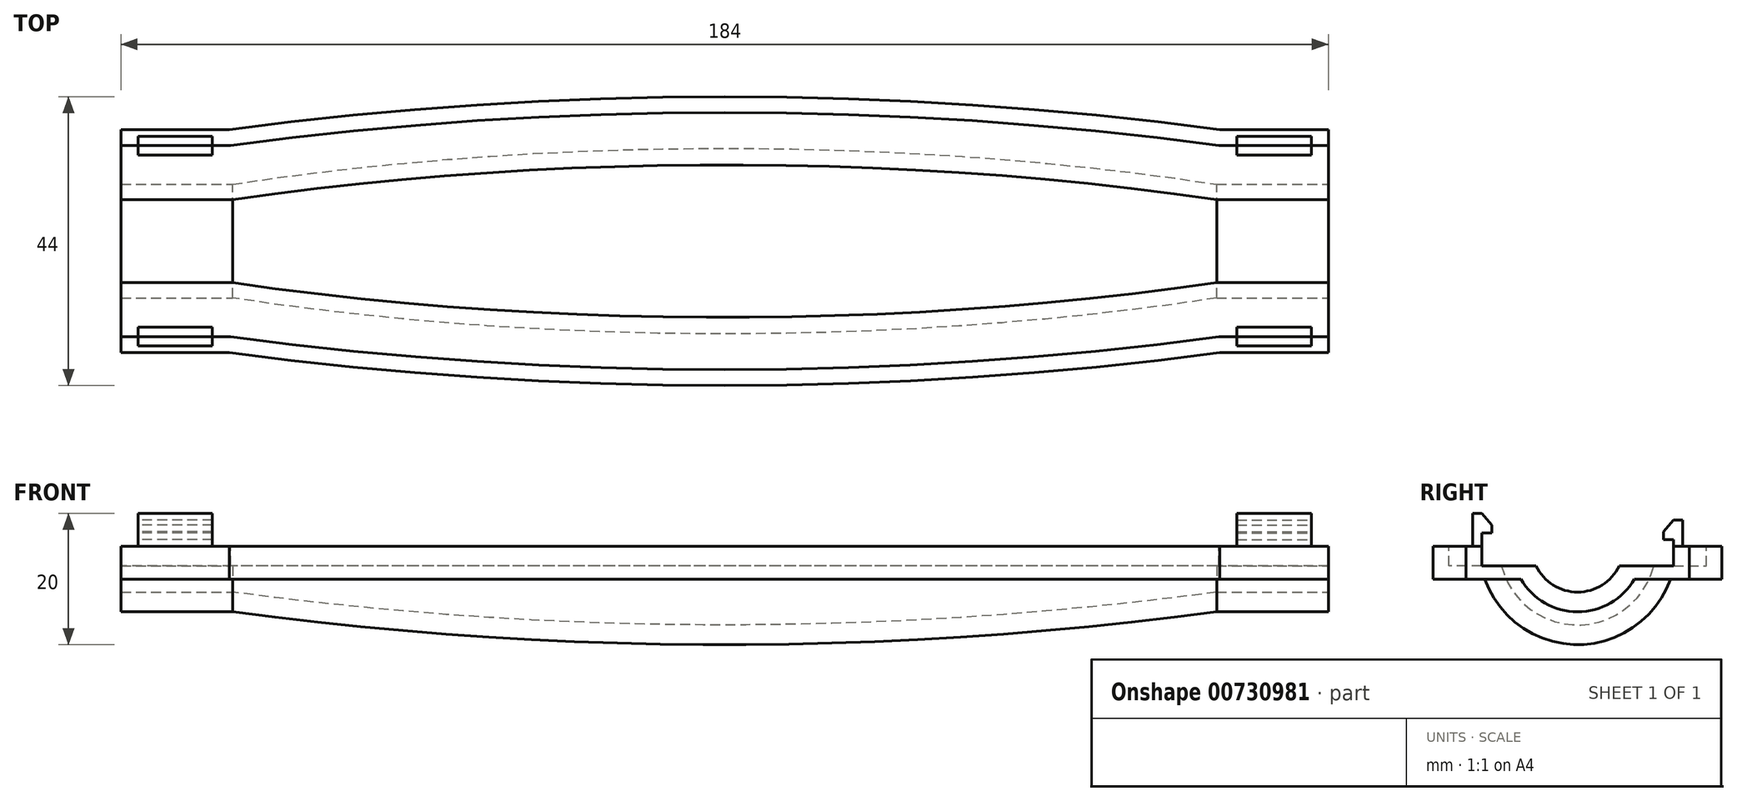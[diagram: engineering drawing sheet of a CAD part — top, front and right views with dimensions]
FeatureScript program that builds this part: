
annotation { "Feature Type Name" : "Feature", "Feature Type Description" : "" }
export const myFeature = defineFeature(function(context is Context, id is Id, definition is map)
    precondition{}
    {
        {
            var Q0;
            Q0=qCreatedBy(makeId("Top.planeOp"),FACE);
            var sketch = newSketch(context, id + "F0", { "sketchPlane" : qUnion([Q0])});
            skLineSegment(sketch, "E0", {"start": v(0, 0) * mm, "end": v(0, 12) * mm, "construction": true});
            skLineSegment(sketch, "E1", {"start": v(0, 0) * mm, "end": v(0, -12) * mm, "construction": true});
            skLineSegment(sketch, "E2", {"start": v(0, 0) * mm, "end": v(-75, 0) * mm, "construction": true});
            skLineSegment(sketch, "E3", {"start": v(0, 0) * mm, "end": v(75, 0) * mm, "construction": true});
            skLineSegment(sketch, "E4", {"start": v(-75, 0) * mm, "end": v(-75, 7) * mm, "construction": true});
            skLineSegment(sketch, "E5", {"start": v(75, 0) * mm, "end": v(75, 7) * mm, "construction": true});
            skArc(sketch, "E6", {"start": v(75, 7) * mm, "mid": v(0, 12) * mm, "end": v(-75, 7) * mm});
            skLineSegment(sketch, "E7", {"start": v(75, 7) * mm, "end": v(92, 7) * mm});
            skLineSegment(sketch, "E8", {"start": v(-75, 7) * mm, "end": v(-92, 7) * mm});
            skLineSegment(sketch, "E9", {"start": v(-92, 7) * mm, "end": v(-92, 10) * mm});
            skLineSegment(sketch, "E10", {"start": v(-92, 10) * mm, "end": v(-75, 10) * mm});
            skLineSegment(sketch, "E11", {"start": v(92, 7) * mm, "end": v(92, 10) * mm});
            skLineSegment(sketch, "E12", {"start": v(92, 10) * mm, "end": v(75, 10) * mm});
            skLineSegment(sketch, "E13", {"start": v(0, 12) * mm, "end": v(0, 15) * mm, "construction": true});
            skArc(sketch, "E14", {"start": v(75, 10) * mm, "mid": v(0, 15) * mm, "end": v(-75, 10) * mm});
            skSolve(sketch);
        }
        {
            var Q0;
            Q0=makeQuery(id+"F0.imprint","IMPRINT",FACE,{"disambiguationData":[TD([[makeQuery(id+"F0.imprint","IMPRINT",EDGE,{"derivedFrom":sQuery(id+"F0.wireOp",EDGE,"E6")}),-1.0]])]});
            var Q1;
            Q1=sQuery(id+"F0.wireOp",EDGE,"E2");
            revolve(context, id + "F1", {"surfaceOperationType" : NewSurfaceOperationType.NEW, "entities" : qUnion([Q0]), "axis" : qUnion([Q1]), "revolveType" : RevolveType.ONE_DIRECTION, "angle" : 180 * degree});
        }
        {
            var Q0;
            Q0=makeQuery(id+"F1.opRevolve","CAP_FACE",FACE,{"disambiguationData":[OSD([sQuery(id+"F0.wireOp",EDGE,"E6"),sQuery(id+"F0.wireOp",EDGE,"E7"),sQuery(id+"F0.wireOp",EDGE,"E8"),sQuery(id+"F0.wireOp",EDGE,"E9"),sQuery(id+"F0.wireOp",EDGE,"E10"),sQuery(id+"F0.wireOp",EDGE,"E11"),sQuery(id+"F0.wireOp",EDGE,"E12"),sQuery(id+"F0.wireOp",EDGE,"E14")])],"isStart":true});
            var sketch = newSketch(context, id + "F2", { "sketchPlane" : qUnion([Q0])});
            skLineSegment(sketch, "E15.0", {"start": v(-92, 17) * mm, "end": v(-75.47, 17) * mm});
            skArc(sketch, "E15.1", {"start": v(75.47, 17) * mm, "mid": v(0, 22) * mm, "end": v(-75.47, 17) * mm});
            skLineSegment(sketch, "E15.2", {"start": v(92, 17) * mm, "end": v(75.47, 17) * mm});
            skLineSegment(sketch, "E16", {"start": v(-92, 17) * mm, "end": v(-92, 10) * mm});
            skLineSegment(sketch, "E17", {"start": v(92, 17) * mm, "end": v(92, 10) * mm});
            skSolve(sketch);
        }
        {
            var Q0;
            Q0=makeQuery(id+"F2.imprint","IMPRINT",FACE,{"disambiguationData":[TD([[makeQuery(id+"F2.imprint","IMPRINT",EDGE,{"derivedFrom":makeQuery(id+"F1.opRevolve","CAP_EDGE",EDGE,{"disambiguationData":[OSD([sQuery(id+"F0.wireOp",EDGE,"E6")])],"isStart":true})}),-1.0]])]});
            var Q1;
            Q1=makeQuery(id+"F2.imprint","IMPRINT",FACE,{"disambiguationData":[TD([[makeQuery(id+"F2.imprint","IMPRINT",EDGE,{"derivedFrom":sQuery(id+"F2.wireOp",EDGE,"E15.0")}),-1.0]])]});
            extrude(context, id + "F3", {"entities" : qUnion([Q0, Q1]), "operationType" : NewBodyOperationType.ADD, "oppositeDirection" : true, "depth" : 5 * mm, "offsetDistance" : 25 * mm});
        }
        {
            var Q0;
            Q0=makeQuery(id+"F1.opRevolve","CAP_FACE",FACE,{"disambiguationData":[OSD([sQuery(id+"F0.wireOp",EDGE,"E6"),sQuery(id+"F0.wireOp",EDGE,"E7"),sQuery(id+"F0.wireOp",EDGE,"E8"),sQuery(id+"F0.wireOp",EDGE,"E9"),sQuery(id+"F0.wireOp",EDGE,"E10"),sQuery(id+"F0.wireOp",EDGE,"E11"),sQuery(id+"F0.wireOp",EDGE,"E12"),sQuery(id+"F0.wireOp",EDGE,"E14")])],"isStart":false});
            var sketch = newSketch(context, id + "F4", { "sketchPlane" : qUnion([Q0])});
            skLineSegment(sketch, "E18.0", {"start": v(-92, -17) * mm, "end": v(-75.47, -17) * mm});
            skArc(sketch, "E18.1", {"start": v(75.47, -17) * mm, "mid": v(0, -22) * mm, "end": v(-75.47, -17) * mm});
            skLineSegment(sketch, "E18.2", {"start": v(92, -17) * mm, "end": v(75.47, -17) * mm});
            skLineSegment(sketch, "E19", {"start": v(-92, -17) * mm, "end": v(-92, -10) * mm});
            skLineSegment(sketch, "E20", {"start": v(92, -17) * mm, "end": v(92, -10) * mm});
            skSolve(sketch);
        }
        {
            var Q0;
            Q0=makeQuery(id+"F4.imprint","IMPRINT",FACE,{"disambiguationData":[TD([[makeQuery(id+"F4.imprint","IMPRINT",EDGE,{"derivedFrom":makeQuery(id+"F1.opRevolve","CAP_EDGE",EDGE,{"disambiguationData":[OSD([sQuery(id+"F0.wireOp",EDGE,"E6")])],"isStart":false})}),1.0]])]});
            var Q1;
            Q1=makeQuery(id+"F4.imprint","IMPRINT",FACE,{"disambiguationData":[TD([[makeQuery(id+"F4.imprint","IMPRINT",EDGE,{"derivedFrom":sQuery(id+"F4.wireOp",EDGE,"E18.0")}),1.0]])]});
            extrude(context, id + "F5", {"entities" : qUnion([Q0, Q1]), "operationType" : NewBodyOperationType.ADD, "oppositeDirection" : true, "depth" : 5 * mm, "offsetDistance" : 25 * mm});
        }
        {
            var Q0;
            {var subQ0=sQuery(id+"F0.wireOp",EDGE,"E11");var subQ1=sQuery(id+"F0.wireOp",EDGE,"E9");var subQ2=sQuery(id+"F0.wireOp",EDGE,"E8");var subQ3=sQuery(id+"F0.wireOp",EDGE,"E7");var subQ4=sQuery(id+"F0.wireOp",EDGE,"E6");Q0=makeQuery(id+"F3.boolean.opBoolean","MERGE",FACE,{"derivedFrom":[makeQuery(id+"F1.opRevolve","CAP_FACE",FACE,{"disambiguationData":[OSD([subQ4,subQ3,subQ2,subQ1,sQuery(id+"F0.wireOp",EDGE,"E10"),subQ0,sQuery(id+"F0.wireOp",EDGE,"E12"),sQuery(id+"F0.wireOp",EDGE,"E14")])],"isStart":true}),makeQuery(id+"F3.opExtrude","CAP_FACE",FACE,{"disambiguationData":[OSD([subQ4,subQ3,subQ2,subQ1,subQ0,sQuery(id+"F2.wireOp",EDGE,"E15.0"),sQuery(id+"F2.wireOp",EDGE,"E15.1"),sQuery(id+"F2.wireOp",EDGE,"E15.2"),sQuery(id+"F2.wireOp",EDGE,"E16"),sQuery(id+"F2.wireOp",EDGE,"E17")])],"isStart":true})]});}
            var sketch = newSketch(context, id + "F6", { "sketchPlane" : qUnion([Q0])});
            skLineSegment(sketch, "E21.0", {"start": v(-92, 14.6) * mm, "end": v(-75.3, 14.6) * mm});
            skArc(sketch, "E21.1", {"start": v(75.3, 14.6) * mm, "mid": v(0, 19.6) * mm, "end": v(-75.3, 14.6) * mm});
            skLineSegment(sketch, "E21.2", {"start": v(92, 14.6) * mm, "end": v(75.3, 14.6) * mm});
            skArc(sketch, "E22.0", {"start": v(75, 8.82) * mm, "mid": v(0, 13.8) * mm, "end": v(-75, 8.82) * mm});
            skLineSegment(sketch, "E23", {"start": v(-75, 7) * mm, "end": v(-75, 8.82) * mm});
            skLineSegment(sketch, "E24", {"start": v(75, 7) * mm, "end": v(75, 8.82) * mm});
            skSolve(sketch);
        }
        {
            var Q0;
            {var subQ7=sQuery(id+"F6.wireOp",EDGE,"E21.0");Q0=makeQuery(id+"F6.imprint","IMPRINT",FACE,{"disambiguationData":[TD([[makeQuery(id+"F6.imprint","IMPRINT",EDGE,{"derivedFrom":subQ7}),-1.0]])]});}
            extrude(context, id + "F7", {"entities" : qUnion([Q0]), "operationType" : NewBodyOperationType.REMOVE, "oppositeDirection" : true, "depth" : 3 * mm, "offsetDistance" : 25 * mm});
        }
        {
            var Q0;
            {var subQ0=sQuery(id+"F0.wireOp",EDGE,"E9");Q0=makeQuery(id+"F5.boolean.opBoolean","MERGE",FACE,{"derivedFrom":[makeQuery(id+"F3.boolean.opBoolean","MERGE",FACE,{"derivedFrom":[makeQuery(id+"F1.opRevolve","SWEPT_FACE",FACE,{"disambiguationData":[OSD([subQ0])]}),makeQuery(id+"F3.opExtrude","SWEPT_FACE",FACE,{"disambiguationData":[OSD([subQ0,sQuery(id+"F2.wireOp",EDGE,"E16")])]})]}),makeQuery(id+"F5.opExtrude","SWEPT_FACE",FACE,{"disambiguationData":[OSD([subQ0,sQuery(id+"F4.wireOp",EDGE,"E19")])]})]});}
            var sketch = newSketch(context, id + "F8", { "sketchPlane" : qUnion([Q0])});
            skLineSegment(sketch, "E25", {"start": v(-7, -3) * mm, "end": v(-6.32, -3) * mm});
            skSolve(sketch);
        }
        {
            var Q0;
            {var subQ0=sQuery(id+"F8.wireOp",EDGE,"E25");Q0=makeQuery(id+"F8.imprint","IMPRINT",FACE,{"disambiguationData":[TD([[makeQuery(id+"F8.imprint","IMPRINT",EDGE,{"derivedFrom":subQ0}),1.0]])]});}
            extrude(context, id + "F9", {"entities" : qUnion([Q0]), "operationType" : NewBodyOperationType.REMOVE, "oppositeDirection" : true, "depth" : 17 * mm, "offsetDistance" : 25 * mm});
        }
        {
            var Q0;
            {var subQ0=sQuery(id+"F0.wireOp",EDGE,"E11");Q0=makeQuery(id+"F5.boolean.opBoolean","MERGE",FACE,{"derivedFrom":[makeQuery(id+"F3.boolean.opBoolean","MERGE",FACE,{"derivedFrom":[makeQuery(id+"F1.opRevolve","SWEPT_FACE",FACE,{"disambiguationData":[OSD([subQ0])]}),makeQuery(id+"F3.opExtrude","SWEPT_FACE",FACE,{"disambiguationData":[OSD([subQ0,sQuery(id+"F2.wireOp",EDGE,"E17")])]})]}),makeQuery(id+"F5.opExtrude","SWEPT_FACE",FACE,{"disambiguationData":[OSD([subQ0,sQuery(id+"F4.wireOp",EDGE,"E20")])]})]});}
            var sketch = newSketch(context, id + "F10", { "sketchPlane" : qUnion([Q0])});
            skLineSegment(sketch, "E26", {"start": v(7, -3) * mm, "end": v(6.32, -3) * mm});
            skSolve(sketch);
        }
        {
            var Q0;
            {var subQ0=sQuery(id+"F10.wireOp",EDGE,"E26");Q0=makeQuery(id+"F10.imprint","IMPRINT",FACE,{"disambiguationData":[TD([[makeQuery(id+"F10.imprint","IMPRINT",EDGE,{"derivedFrom":subQ0}),-1.0]])]});}
            extrude(context, id + "F11", {"entities" : qUnion([Q0]), "operationType" : NewBodyOperationType.REMOVE, "oppositeDirection" : true, "depth" : 17 * mm, "offsetDistance" : 25 * mm});
        }
        {
            var Q0;
            {var subQ0=sQuery(id+"F0.wireOp",EDGE,"E11");var subQ1=sQuery(id+"F0.wireOp",EDGE,"E9");var subQ2=sQuery(id+"F0.wireOp",EDGE,"E8");var subQ3=sQuery(id+"F0.wireOp",EDGE,"E7");var subQ4=sQuery(id+"F0.wireOp",EDGE,"E6");Q0=makeQuery(id+"F5.boolean.opBoolean","MERGE",FACE,{"derivedFrom":[makeQuery(id+"F1.opRevolve","CAP_FACE",FACE,{"disambiguationData":[OSD([subQ4,subQ3,subQ2,subQ1,sQuery(id+"F0.wireOp",EDGE,"E10"),subQ0,sQuery(id+"F0.wireOp",EDGE,"E12"),sQuery(id+"F0.wireOp",EDGE,"E14")])],"isStart":false}),makeQuery(id+"F5.opExtrude","CAP_FACE",FACE,{"disambiguationData":[OSD([subQ4,subQ3,subQ2,subQ1,subQ0,sQuery(id+"F4.wireOp",EDGE,"E18.0"),sQuery(id+"F4.wireOp",EDGE,"E18.1"),sQuery(id+"F4.wireOp",EDGE,"E18.2"),sQuery(id+"F4.wireOp",EDGE,"E19"),sQuery(id+"F4.wireOp",EDGE,"E20")])],"isStart":true})]});}
            var sketch = newSketch(context, id + "F12", { "sketchPlane" : qUnion([Q0])});
            skLineSegment(sketch, "E27.0", {"start": v(-92, -14.6) * mm, "end": v(-75.3, -14.6) * mm});
            skArc(sketch, "E27.1", {"start": v(75.3, -14.6) * mm, "mid": v(0, -19.6) * mm, "end": v(-75.3, -14.6) * mm});
            skLineSegment(sketch, "E27.2", {"start": v(92, -14.6) * mm, "end": v(75.3, -14.6) * mm});
            skLineSegment(sketch, "E28.0", {"start": v(-75.12, -8.8) * mm, "end": v(-92, -8.8) * mm});
            skArc(sketch, "E28.1", {"start": v(75.12, -8.8) * mm, "mid": v(0, -13.8) * mm, "end": v(-75.12, -8.8) * mm});
            skLineSegment(sketch, "E28.2", {"start": v(75.12, -8.8) * mm, "end": v(92, -8.8) * mm});
            skLineSegment(sketch, "E29", {"start": v(75, -7) * mm, "end": v(75, -8.82) * mm});
            skLineSegment(sketch, "E30", {"start": v(-75, -7) * mm, "end": v(-75, -8.82) * mm});
            skSolve(sketch);
        }
        {
            var Q0;
            {var subQ3=sQuery(id+"F12.wireOp",EDGE,"E28.0");Q0=makeQuery(id+"F12.imprint","IMPRINT",FACE,{"disambiguationData":[TD([[makeQuery(id+"F12.imprint","IMPRINT",EDGE,{"derivedFrom":subQ3}),-1.0]])]});}
            var Q1;
            {var subQ2=sQuery(id+"F12.wireOp",EDGE,"E27.0");Q1=makeQuery(id+"F12.imprint","IMPRINT",FACE,{"disambiguationData":[TD([[makeQuery(id+"F12.imprint","IMPRINT",EDGE,{"derivedFrom":subQ2}),1.0]])]});}
            var Q2;
            {var subQ4=sQuery(id+"F12.wireOp",EDGE,"E28.2");Q2=makeQuery(id+"F12.imprint","IMPRINT",FACE,{"disambiguationData":[TD([[makeQuery(id+"F12.imprint","IMPRINT",EDGE,{"derivedFrom":subQ4}),1.0]])]});}
            extrude(context, id + "F13", {"entities" : qUnion([Q0, Q1, Q2]), "operationType" : NewBodyOperationType.REMOVE, "oppositeDirection" : true, "depth" : 3 * mm, "offsetDistance" : 25 * mm});
        }
        {
            var Q0;
            {var subQ0=sQuery(id+"F0.wireOp",EDGE,"E9");Q0=makeQuery(id+"F5.boolean.opBoolean","MERGE",FACE,{"derivedFrom":[makeQuery(id+"F3.boolean.opBoolean","MERGE",FACE,{"derivedFrom":[makeQuery(id+"F1.opRevolve","SWEPT_FACE",FACE,{"disambiguationData":[OSD([subQ0])]}),makeQuery(id+"F3.opExtrude","SWEPT_FACE",FACE,{"disambiguationData":[OSD([subQ0,sQuery(id+"F2.wireOp",EDGE,"E16")])]})]}),makeQuery(id+"F5.opExtrude","SWEPT_FACE",FACE,{"disambiguationData":[OSD([subQ0,sQuery(id+"F4.wireOp",EDGE,"E19")])]})]});}
            var sketch = newSketch(context, id + "F14", { "sketchPlane" : qUnion([Q0])});
            skLineSegment(sketch, "E31", {"start": v(7, -3) * mm, "end": v(6.32, -3) * mm});
            skSolve(sketch);
        }
        {
            var Q0;
            {var subQ0=sQuery(id+"F14.wireOp",EDGE,"E31");Q0=makeQuery(id+"F14.imprint","IMPRINT",FACE,{"disambiguationData":[TD([[makeQuery(id+"F14.imprint","IMPRINT",EDGE,{"derivedFrom":subQ0}),-1.0]])]});}
            extrude(context, id + "F15", {"entities" : qUnion([Q0]), "operationType" : NewBodyOperationType.REMOVE, "oppositeDirection" : true, "depth" : 17 * mm, "offsetDistance" : 25 * mm});
        }
        {
            var Q0;
            {var subQ0=sQuery(id+"F0.wireOp",EDGE,"E11");Q0=makeQuery(id+"F5.boolean.opBoolean","MERGE",FACE,{"derivedFrom":[makeQuery(id+"F3.boolean.opBoolean","MERGE",FACE,{"derivedFrom":[makeQuery(id+"F1.opRevolve","SWEPT_FACE",FACE,{"disambiguationData":[OSD([subQ0])]}),makeQuery(id+"F3.opExtrude","SWEPT_FACE",FACE,{"disambiguationData":[OSD([subQ0,sQuery(id+"F2.wireOp",EDGE,"E17")])]})]}),makeQuery(id+"F5.opExtrude","SWEPT_FACE",FACE,{"disambiguationData":[OSD([subQ0,sQuery(id+"F4.wireOp",EDGE,"E20")])]})]});}
            var sketch = newSketch(context, id + "F16", { "sketchPlane" : qUnion([Q0])});
            skLineSegment(sketch, "E32", {"start": v(-7, -3) * mm, "end": v(-6.32, -3) * mm});
            skSolve(sketch);
        }
        {
            var Q0;
            {var subQ0=sQuery(id+"F16.wireOp",EDGE,"E32");Q0=makeQuery(id+"F16.imprint","IMPRINT",FACE,{"disambiguationData":[TD([[makeQuery(id+"F16.imprint","IMPRINT",EDGE,{"derivedFrom":subQ0}),1.0]])]});}
            extrude(context, id + "F17", {"entities" : qUnion([Q0]), "operationType" : NewBodyOperationType.REMOVE, "oppositeDirection" : true, "depth" : 17 * mm, "offsetDistance" : 25 * mm});
        }
        {
            var Q0;
            {var subQ0=sQuery(id+"F0.wireOp",EDGE,"E8");var subQ1=sQuery(id+"F0.wireOp",EDGE,"E7");var subQ2=sQuery(id+"F0.wireOp",EDGE,"E6");var subQ3=sQuery(id+"F0.wireOp",EDGE,"E11");var subQ4=sQuery(id+"F0.wireOp",EDGE,"E9");Q0=makeQuery(id+"F7.boolean.opBoolean","SPLIT",FACE,{"disambiguationData":[TD([makeQuery(id+"F1.opRevolve","SWEPT_FACE",FACE,{"disambiguationData":[OSD([subQ2])]})])],"derivedFrom":makeQuery(id+"F3.boolean.opBoolean","MERGE",FACE,{"derivedFrom":[makeQuery(id+"F1.opRevolve","CAP_FACE",FACE,{"disambiguationData":[OSD([subQ2,subQ1,subQ0,subQ4,sQuery(id+"F0.wireOp",EDGE,"E10"),subQ3,sQuery(id+"F0.wireOp",EDGE,"E12"),sQuery(id+"F0.wireOp",EDGE,"E14")])],"isStart":true}),makeQuery(id+"F3.opExtrude","CAP_FACE",FACE,{"disambiguationData":[OSD([subQ2,subQ1,subQ0,subQ4,subQ3,sQuery(id+"F2.wireOp",EDGE,"E15.0"),sQuery(id+"F2.wireOp",EDGE,"E15.1"),sQuery(id+"F2.wireOp",EDGE,"E15.2"),sQuery(id+"F2.wireOp",EDGE,"E16"),sQuery(id+"F2.wireOp",EDGE,"E17")])],"isStart":true})]})});}
            var sketch = newSketch(context, id + "F18", { "sketchPlane" : qUnion([Q0])});
            skLineSegment(sketch, "E33", {"start": v(-75, 8.82) * mm, "end": v(-75, 5.4) * mm});
            skLineSegment(sketch, "E34", {"start": v(-75, 5.4) * mm, "end": v(75, 5.4) * mm});
            skLineSegment(sketch, "E35", {"start": v(75, 5.4) * mm, "end": v(75, 8.82) * mm});
            skSolve(sketch);
        }
        {
            var Q0;
            {var subQ2=sQuery(id+"F18.wireOp",EDGE,"E34");Q0=makeQuery(id+"F18.imprint","IMPRINT",FACE,{"disambiguationData":[TD([[makeQuery(id+"F18.imprint","IMPRINT",EDGE,{"derivedFrom":subQ2}),1.0]])]});}
            var Q1;
            {var subQ2=makeQuery(id+"F1.opRevolve","CAP_EDGE",EDGE,{"disambiguationData":[OSD([sQuery(id+"F0.wireOp",EDGE,"E6")])],"isStart":true});Q1=makeQuery(id+"F18.imprint","IMPRINT",FACE,{"disambiguationData":[TD([[makeQuery(id+"F18.imprint","IMPRINT",EDGE,{"derivedFrom":subQ2}),-1.0]])]});}
            extrude(context, id + "F19", {"entities" : qUnion([Q0, Q1]), "operationType" : NewBodyOperationType.REMOVE, "oppositeDirection" : true, "depth" : 3 * mm, "offsetDistance" : 25 * mm});
        }
        {
            var Q0;
            {var subQ0=sQuery(id+"F0.wireOp",EDGE,"E8");var subQ1=sQuery(id+"F0.wireOp",EDGE,"E7");var subQ2=sQuery(id+"F0.wireOp",EDGE,"E6");var subQ3=sQuery(id+"F0.wireOp",EDGE,"E11");var subQ4=sQuery(id+"F0.wireOp",EDGE,"E9");Q0=makeQuery(id+"F13.boolean.opBoolean","SPLIT",FACE,{"disambiguationData":[TD([makeQuery(id+"F1.opRevolve","SWEPT_FACE",FACE,{"disambiguationData":[OSD([subQ2])]})])],"derivedFrom":makeQuery(id+"F5.boolean.opBoolean","MERGE",FACE,{"derivedFrom":[makeQuery(id+"F1.opRevolve","CAP_FACE",FACE,{"disambiguationData":[OSD([subQ2,subQ1,subQ0,subQ4,sQuery(id+"F0.wireOp",EDGE,"E10"),subQ3,sQuery(id+"F0.wireOp",EDGE,"E12"),sQuery(id+"F0.wireOp",EDGE,"E14")])],"isStart":false}),makeQuery(id+"F5.opExtrude","CAP_FACE",FACE,{"disambiguationData":[OSD([subQ2,subQ1,subQ0,subQ4,subQ3,sQuery(id+"F4.wireOp",EDGE,"E18.0"),sQuery(id+"F4.wireOp",EDGE,"E18.1"),sQuery(id+"F4.wireOp",EDGE,"E18.2"),sQuery(id+"F4.wireOp",EDGE,"E19"),sQuery(id+"F4.wireOp",EDGE,"E20")])],"isStart":true})]})});}
            var sketch = newSketch(context, id + "F20", { "sketchPlane" : qUnion([Q0])});
            skLineSegment(sketch, "E36", {"start": v(-75, -8.82) * mm, "end": v(-75, -5.3) * mm});
            skLineSegment(sketch, "E37", {"start": v(-75, -5.3) * mm, "end": v(75, -5.3) * mm});
            skLineSegment(sketch, "E38", {"start": v(75, -5.3) * mm, "end": v(75, -8.82) * mm});
            skSolve(sketch);
        }
        {
            var Q0;
            {var subQ2=sQuery(id+"F20.wireOp",EDGE,"E37");Q0=makeQuery(id+"F20.imprint","IMPRINT",FACE,{"disambiguationData":[TD([[makeQuery(id+"F20.imprint","IMPRINT",EDGE,{"derivedFrom":subQ2}),-1.0]])]});}
            var Q1;
            {var subQ2=makeQuery(id+"F1.opRevolve","CAP_EDGE",EDGE,{"disambiguationData":[OSD([sQuery(id+"F0.wireOp",EDGE,"E6")])],"isStart":false});Q1=makeQuery(id+"F20.imprint","IMPRINT",FACE,{"disambiguationData":[TD([[makeQuery(id+"F20.imprint","IMPRINT",EDGE,{"derivedFrom":subQ2}),1.0]])]});}
            extrude(context, id + "F21", {"entities" : qUnion([Q0, Q1]), "operationType" : NewBodyOperationType.REMOVE, "oppositeDirection" : true, "depth" : 3 * mm, "offsetDistance" : 25 * mm});
        }
        {
            var Q0;
            {var subQ0=sQuery(id+"F0.wireOp",EDGE,"E11");var subQ1=sQuery(id+"F2.wireOp",EDGE,"E15.1");var subQ2=sQuery(id+"F0.wireOp",EDGE,"E9");var subQ3=sQuery(id+"F2.wireOp",EDGE,"E16");var subQ4=sQuery(id+"F2.wireOp",EDGE,"E15.2");var subQ5=sQuery(id+"F2.wireOp",EDGE,"E17");var subQ6=sQuery(id+"F2.wireOp",EDGE,"E15.0");var subQ7=sQuery(id+"F0.wireOp",EDGE,"E8");var subQ8=sQuery(id+"F0.wireOp",EDGE,"E7");var subQ9=sQuery(id+"F0.wireOp",EDGE,"E6");Q0=makeQuery(id+"F7.boolean.opBoolean","SPLIT",FACE,{"disambiguationData":[TD([makeQuery(id+"F1.opRevolve","SWEPT_FACE",FACE,{"disambiguationData":[OSD([subQ2])]})])],"derivedFrom":makeQuery(id+"F3.boolean.opBoolean","MERGE",FACE,{"derivedFrom":[makeQuery(id+"F1.opRevolve","CAP_FACE",FACE,{"disambiguationData":[OSD([subQ9,subQ8,subQ7,subQ2,sQuery(id+"F0.wireOp",EDGE,"E10"),subQ0,sQuery(id+"F0.wireOp",EDGE,"E12"),sQuery(id+"F0.wireOp",EDGE,"E14")])],"isStart":true}),makeQuery(id+"F3.opExtrude","CAP_FACE",FACE,{"disambiguationData":[OSD([subQ9,subQ8,subQ7,subQ2,subQ0,subQ6,subQ1,subQ4,subQ3,subQ5])],"isStart":true})]})});}
            var sketch = newSketch(context, id + "F22", { "sketchPlane" : qUnion([Q0])});
            skLineSegment(sketch, "E39", {"start": v(78.07, 17) * mm, "end": v(78.07, 14.6) * mm});
            skLineSegment(sketch, "E40", {"start": v(89.4, 17) * mm, "end": v(89.4, 14.6) * mm});
            skLineSegment(sketch, "E41", {"start": v(78.07, 16) * mm, "end": v(89.4, 16) * mm});
            skLineSegment(sketch, "E42", {"start": v(-78.07, 14.6) * mm, "end": v(-78.07, 17) * mm});
            skLineSegment(sketch, "E43", {"start": v(-89.4, 14.6) * mm, "end": v(-89.4, 17) * mm});
            skLineSegment(sketch, "E44", {"start": v(-78.07, 16) * mm, "end": v(-89.4, 16) * mm});
            skSolve(sketch);
        }
        {
            var Q0;
            {var subQ3=sQuery(id+"F22.wireOp",EDGE,"E41");Q0=makeQuery(id+"F22.imprint","IMPRINT",FACE,{"disambiguationData":[TD([[makeQuery(id+"F22.imprint","IMPRINT",EDGE,{"derivedFrom":subQ3}),-1.0]])]});}
            var Q1;
            {var subQ3=sQuery(id+"F22.wireOp",EDGE,"E44");Q1=makeQuery(id+"F22.imprint","IMPRINT",FACE,{"disambiguationData":[TD([[makeQuery(id+"F22.imprint","IMPRINT",EDGE,{"derivedFrom":subQ3}),1.0]])]});}
            extrude(context, id + "F23", {"entities" : qUnion([Q0, Q1]), "operationType" : NewBodyOperationType.ADD, "depth" : 4 * mm, "offsetDistance" : 25 * mm});
        }
        {
            var Q0;
            {var subQ0=sQuery(id+"F4.wireOp",EDGE,"E20");var subQ1=sQuery(id+"F0.wireOp",EDGE,"E11");var subQ2=sQuery(id+"F4.wireOp",EDGE,"E19");var subQ3=sQuery(id+"F0.wireOp",EDGE,"E9");var subQ4=sQuery(id+"F4.wireOp",EDGE,"E18.2");var subQ5=sQuery(id+"F4.wireOp",EDGE,"E18.1");var subQ6=sQuery(id+"F4.wireOp",EDGE,"E18.0");var subQ7=sQuery(id+"F0.wireOp",EDGE,"E8");var subQ8=sQuery(id+"F0.wireOp",EDGE,"E7");var subQ9=sQuery(id+"F0.wireOp",EDGE,"E6");Q0=makeQuery(id+"F13.boolean.opBoolean","SPLIT",FACE,{"disambiguationData":[TD([makeQuery(id+"F1.opRevolve","SWEPT_FACE",FACE,{"disambiguationData":[OSD([subQ3])]})])],"derivedFrom":makeQuery(id+"F5.boolean.opBoolean","MERGE",FACE,{"derivedFrom":[makeQuery(id+"F1.opRevolve","CAP_FACE",FACE,{"disambiguationData":[OSD([subQ9,subQ8,subQ7,subQ3,sQuery(id+"F0.wireOp",EDGE,"E10"),subQ1,sQuery(id+"F0.wireOp",EDGE,"E12"),sQuery(id+"F0.wireOp",EDGE,"E14")])],"isStart":false}),makeQuery(id+"F5.opExtrude","CAP_FACE",FACE,{"disambiguationData":[OSD([subQ9,subQ8,subQ7,subQ3,subQ1,subQ6,subQ5,subQ4,subQ2,subQ0])],"isStart":true})]})});}
            var sketch = newSketch(context, id + "F24", { "sketchPlane" : qUnion([Q0])});
            skLineSegment(sketch, "E45", {"start": v(-89.4, -17) * mm, "end": v(-89.4, -14.6) * mm});
            skLineSegment(sketch, "E46", {"start": v(-78.07, -17) * mm, "end": v(-78.07, -14.6) * mm});
            skLineSegment(sketch, "E47", {"start": v(89.4, -14.6) * mm, "end": v(89.4, -17) * mm});
            skLineSegment(sketch, "E48", {"start": v(78.07, -14.6) * mm, "end": v(78.07, -17) * mm});
            skSolve(sketch);
        }
        {
            var Q0;
            {var subQ0=sQuery(id+"F24.wireOp",EDGE,"E47");Q0=makeQuery(id+"F24.imprint","IMPRINT",FACE,{"disambiguationData":[TD([[makeQuery(id+"F24.imprint","IMPRINT",EDGE,{"derivedFrom":subQ0}),-1.0]])]});}
            var Q1;
            {var subQ0=sQuery(id+"F24.wireOp",EDGE,"E45");Q1=makeQuery(id+"F24.imprint","IMPRINT",FACE,{"disambiguationData":[TD([[makeQuery(id+"F24.imprint","IMPRINT",EDGE,{"derivedFrom":subQ0}),-1.0]])]});}
            extrude(context, id + "F25", {"entities" : qUnion([Q0, Q1]), "operationType" : NewBodyOperationType.ADD, "depth" : 5 * mm, "offsetDistance" : 25 * mm});
        }
        {
            var Q0;
            Q0=makeQuery(id+"F25.opExtrude","SWEPT_FACE",FACE,{"disambiguationData":[OSD([sQuery(id+"F24.wireOp",EDGE,"E45")])]});
            var sketch = newSketch(context, id + "F26", { "sketchPlane" : qUnion([Q0])});
            skLineSegment(sketch, "E49", {"start": v(13.1, 2) * mm, "end": v(13.1, 3.2) * mm});
            skLineSegment(sketch, "E50", {"start": v(13.1, 3.2) * mm, "end": v(14.6, 5) * mm});
            skLineSegment(sketch, "E51", {"start": v(13.1, 2) * mm, "end": v(14.6, 2) * mm});
            skSolve(sketch);
        }
        {
            var Q0;
            Q0=makeQuery(id+"F26.imprint","IMPRINT",FACE,{"disambiguationData":[TD([[makeQuery(id+"F26.imprint","IMPRINT",EDGE,{"derivedFrom":sQuery(id+"F26.wireOp",EDGE,"E49")}),-1.0]])]});
            var Q1;
            Q1=makeQuery(id+"F25.opExtrude","SWEPT_FACE",FACE,{"disambiguationData":[OSD([sQuery(id+"F24.wireOp",EDGE,"E46")])]});
            extrude(context, id + "F27", {"entities" : qUnion([Q0]), "operationType" : NewBodyOperationType.ADD, "endBound" : BoundingType.UP_TO_SURFACE, "oppositeDirection" : true, "depth" : 11.34 * mm, "endBoundEntityFace" : qUnion([Q1]), "offsetDistance" : 25 * mm});
        }
        {
            var Q0;
            {var subQ0=sQuery(id+"F4.wireOp",EDGE,"E18.0");Q0=makeQuery(id+"F25.boolean.opBoolean","MERGE",FACE,{"derivedFrom":[makeQuery(id+"F5.opExtrude","SWEPT_FACE",FACE,{"disambiguationData":[OSD([subQ0])]}),makeQuery(id+"F25.opExtrude","SWEPT_FACE",FACE,{"disambiguationData":[OSD([subQ0])]})]});}
            var sketch = newSketch(context, id + "F28", { "sketchPlane" : qUnion([Q0])});
            skLineSegment(sketch, "E52", {"start": v(-89.4, 0) * mm, "end": v(-78.07, 0) * mm});
            skSolve(sketch);
        }
        {
            var Q0;
            Q0=makeQuery(id+"F28.imprint","IMPRINT",FACE,{"disambiguationData":[TD([[makeQuery(id+"F28.imprint","IMPRINT",EDGE,{"derivedFrom":sQuery(id+"F28.wireOp",EDGE,"E52")}),1.0]])]});
            extrude(context, id + "F29", {"entities" : qUnion([Q0]), "operationType" : NewBodyOperationType.REMOVE, "oppositeDirection" : true, "depth" : 1 * mm, "offsetDistance" : 25 * mm});
        }
        {
            var Q0;
            Q0=makeQuery(id+"F25.opExtrude","SWEPT_FACE",FACE,{"disambiguationData":[OSD([sQuery(id+"F24.wireOp",EDGE,"E47")])]});
            var sketch = newSketch(context, id + "F30", { "sketchPlane" : qUnion([Q0])});
            skLineSegment(sketch, "E53", {"start": v(-14.6, 2) * mm, "end": v(-13.1, 2) * mm});
            skLineSegment(sketch, "E54", {"start": v(-13.1, 3.2) * mm, "end": v(-14.6, 5) * mm});
            skLineSegment(sketch, "E55", {"start": v(-14.6, 5) * mm, "end": v(-14.6, 2) * mm});
            skLineSegment(sketch, "E56", {"start": v(-13.1, 3.2) * mm, "end": v(-13.1, 2) * mm});
            skSolve(sketch);
        }
        {
            var Q0;
            Q0=makeQuery(id+"F30.imprint","IMPRINT",FACE,{"disambiguationData":[TD([[makeQuery(id+"F30.imprint","IMPRINT",EDGE,{"derivedFrom":sQuery(id+"F30.wireOp",EDGE,"E53")}),1.0]])]});
            var Q1;
            Q1=makeQuery(id+"F25.opExtrude","SWEPT_FACE",FACE,{"disambiguationData":[OSD([sQuery(id+"F24.wireOp",EDGE,"E48")])]});
            extrude(context, id + "F31", {"entities" : qUnion([Q0]), "operationType" : NewBodyOperationType.ADD, "endBound" : BoundingType.UP_TO_SURFACE, "oppositeDirection" : true, "depth" : 25 * mm, "endBoundEntityFace" : qUnion([Q1]), "offsetDistance" : 25 * mm});
        }
        {
            var Q0;
            {var subQ0=sQuery(id+"F4.wireOp",EDGE,"E18.2");Q0=makeQuery(id+"F25.boolean.opBoolean","MERGE",FACE,{"derivedFrom":[makeQuery(id+"F5.opExtrude","SWEPT_FACE",FACE,{"disambiguationData":[OSD([subQ0])]}),makeQuery(id+"F25.opExtrude","SWEPT_FACE",FACE,{"disambiguationData":[OSD([subQ0])]})]});}
            var sketch = newSketch(context, id + "F32", { "sketchPlane" : qUnion([Q0])});
            skLineSegment(sketch, "E57", {"start": v(78.07, 0) * mm, "end": v(89.4, 0) * mm});
            skSolve(sketch);
        }
        {
            var Q0;
            Q0=makeQuery(id+"F32.imprint","IMPRINT",FACE,{"disambiguationData":[TD([[makeQuery(id+"F32.imprint","IMPRINT",EDGE,{"derivedFrom":sQuery(id+"F32.wireOp",EDGE,"E57")}),1.0]])]});
            extrude(context, id + "F33", {"entities" : qUnion([Q0]), "operationType" : NewBodyOperationType.REMOVE, "oppositeDirection" : true, "depth" : 1 * mm, "offsetDistance" : 25 * mm});
        }
        {
            var Q0;
            Q0=makeQuery(id+"F23.opExtrude","SWEPT_FACE",FACE,{"disambiguationData":[OSD([sQuery(id+"F22.wireOp",EDGE,"E40")])]});
            var sketch = newSketch(context, id + "F34", { "sketchPlane" : qUnion([Q0])});
            skLineSegment(sketch, "E58", {"start": v(14.6, 1) * mm, "end": v(13.1, 1) * mm});
            skLineSegment(sketch, "E59", {"start": v(13.1, 1) * mm, "end": v(13.1, 2.2) * mm});
            skLineSegment(sketch, "E60", {"start": v(13.1, 2.2) * mm, "end": v(14.6, 4) * mm});
            skSolve(sketch);
        }
        {
            var Q0;
            {var subQ0=sQuery(id+"F34.wireOp",EDGE,"E58");Q0=makeQuery(id+"F34.imprint","IMPRINT",FACE,{"disambiguationData":[TD([[makeQuery(id+"F34.imprint","IMPRINT",EDGE,{"derivedFrom":subQ0}),-1.0]])]});}
            var Q1;
            Q1=makeQuery(id+"F23.opExtrude","SWEPT_FACE",FACE,{"disambiguationData":[OSD([sQuery(id+"F22.wireOp",EDGE,"E39")])]});
            extrude(context, id + "F35", {"entities" : qUnion([Q0]), "operationType" : NewBodyOperationType.ADD, "endBound" : BoundingType.UP_TO_SURFACE, "oppositeDirection" : true, "depth" : 25 * mm, "endBoundEntityFace" : qUnion([Q1]), "offsetDistance" : 25 * mm});
        }
        {
            var Q0;
            Q0=makeQuery(id+"F23.opExtrude","SWEPT_FACE",FACE,{"disambiguationData":[OSD([sQuery(id+"F22.wireOp",EDGE,"E43")])]});
            var sketch = newSketch(context, id + "F36", { "sketchPlane" : qUnion([Q0])});
            skLineSegment(sketch, "E61", {"start": v(-14.6, 1) * mm, "end": v(-13.1, 1) * mm});
            skLineSegment(sketch, "E62", {"start": v(-13.1, 1) * mm, "end": v(-13.1, 2.2) * mm});
            skLineSegment(sketch, "E63", {"start": v(-13.1, 2.2) * mm, "end": v(-14.6, 4) * mm});
            skLineSegment(sketch, "E64", {"start": v(-14.6, 4) * mm, "end": v(-14.6, 1) * mm});
            skSolve(sketch);
        }
        {
            var Q0;
            Q0=makeQuery(id+"F36.imprint","IMPRINT",FACE,{"disambiguationData":[TD([[makeQuery(id+"F36.imprint","IMPRINT",EDGE,{"derivedFrom":sQuery(id+"F36.wireOp",EDGE,"E61")}),1.0]])]});
            var Q1;
            Q1=makeQuery(id+"F23.opExtrude","SWEPT_FACE",FACE,{"disambiguationData":[OSD([sQuery(id+"F22.wireOp",EDGE,"E42")])]});
            extrude(context, id + "F37", {"entities" : qUnion([Q0]), "operationType" : NewBodyOperationType.ADD, "endBound" : BoundingType.UP_TO_SURFACE, "oppositeDirection" : true, "depth" : 25 * mm, "endBoundEntityFace" : qUnion([Q1]), "offsetDistance" : 25 * mm});
        }
    });
